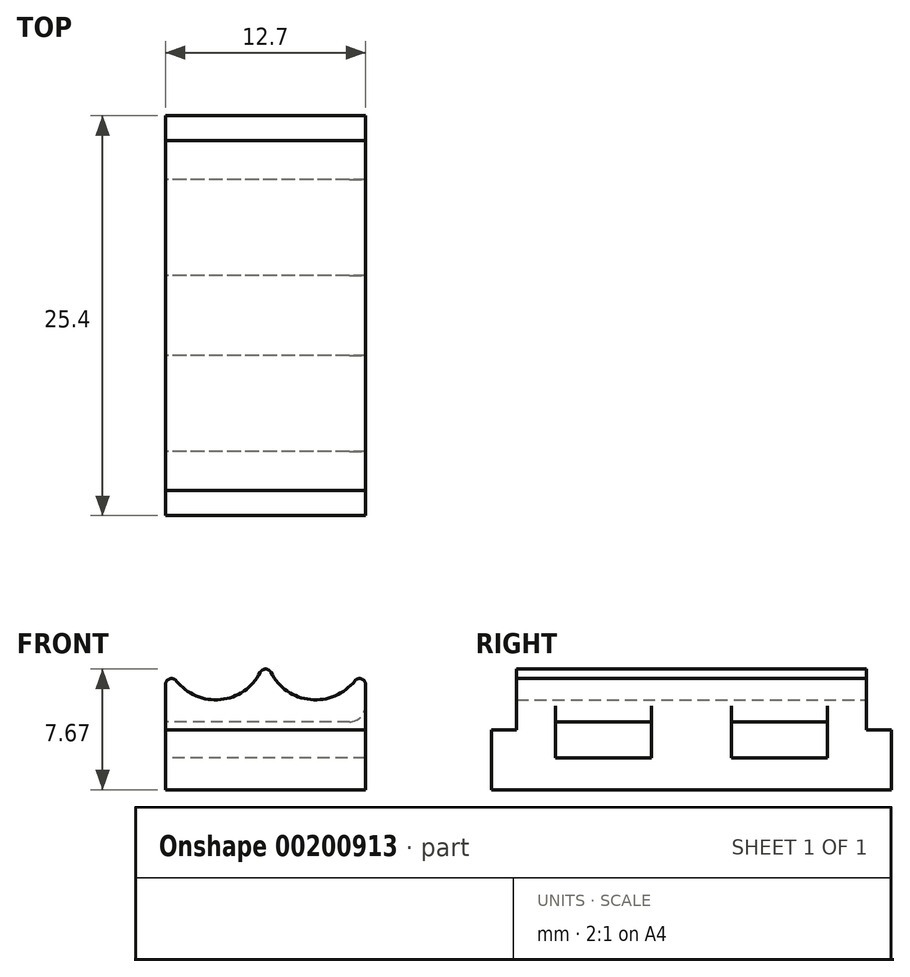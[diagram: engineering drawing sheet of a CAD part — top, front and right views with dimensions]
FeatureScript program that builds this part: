
annotation { "Feature Type Name" : "Feature", "Feature Type Description" : "" }
export const myFeature = defineFeature(function(context is Context, id is Id, definition is map)
    precondition{}
    {
        {
            var Q0;
            Q0=qCreatedBy(makeId("Top.planeOp"),FACE);
            var sketch = newSketch(context, id + "F0", { "sketchPlane" : qUnion([Q0])});
            skLineSegment(sketch, "E0.bottom", {"start": v(6.35, 12.7) * mm, "end": v(-6.35, 12.7) * mm});
            skLineSegment(sketch, "E0.top", {"start": v(6.35, -12.7) * mm, "end": v(-6.35, -12.7) * mm});
            skLineSegment(sketch, "E0.left", {"start": v(6.35, 12.7) * mm, "end": v(6.35, -12.7) * mm});
            skLineSegment(sketch, "E0.right", {"start": v(-6.35, 12.7) * mm, "end": v(-6.35, -12.7) * mm});
            skPoint(sketch, "E0.middle", {"position": v(0, 0) * mm});
            skSolve(sketch);
        }
        {
            var Q0;
            Q0=makeQuery(id+"F0.imprint","IMPRINT",FACE,{"disambiguationData":[TD([[makeQuery(id+"F0.imprint","IMPRINT",EDGE,{"derivedFrom":sQuery(id+"F0.wireOp",EDGE,"E0.bottom")}),1.0]])]});
            extrude(context, id + "F1", {"entities" : qUnion([Q0]), "depth" : 3.8 * mm});
        }
        {
            var Q0;
            Q0=qCreatedBy(makeId("Front.planeOp"),FACE);
            var sketch = newSketch(context, id + "F2", { "sketchPlane" : qUnion([Q0])});
            skArc(sketch, "E1", {"start": v(0, 8.9) * mm, "mid": v(3.18, 5.72) * mm, "end": v(6.35, 8.9) * mm});
            skLineSegment(sketch, "E2", {"start": v(6.35, 8.9) * mm, "end": v(6.35, 3.81) * mm});
            skPoint(sketch, "E3.0", {"position": v(6.35, 3.81) * mm});
            skArc(sketch, "E4.MirrorC", {"start": v(0, 8.9) * mm, "mid": v(-3.18, 5.72) * mm, "end": v(-6.35, 8.9) * mm});
            skLineSegment(sketch, "E5.MirrorCS", {"start": v(-6.35, 8.9) * mm, "end": v(-6.35, 3.81) * mm});
            skLineSegment(sketch, "E6", {"start": v(6.35, 3.81) * mm, "end": v(-6.35, 3.81) * mm});
            skSolve(sketch);
        }
        {
            var Q0;
            Q0=makeQuery(id+"F2.imprint","IMPRINT",FACE,{"disambiguationData":[TD([[makeQuery(id+"F2.imprint","IMPRINT",EDGE,{"derivedFrom":sQuery(id+"F2.wireOp",EDGE,"E1")}),-1.0]])]});
            extrude(context, id + "F3", {"entities" : qUnion([Q0]), "operationType" : NewBodyOperationType.ADD, "endBound" : BoundingType.SYMMETRIC, "depth" : 22.22 * mm});
        }
        {
            var Q0;
            Q0=makeQuery(id+"F3.boolean.opBoolean","MERGE",FACE,{"derivedFrom":[makeQuery(id+"F1.opExtrude","SWEPT_FACE",FACE,{"disambiguationData":[OSD([sQuery(id+"F0.wireOp",EDGE,"E0.right")])]}),makeQuery(id+"F3.opExtrude","SWEPT_FACE",FACE,{"disambiguationData":[OSD([sQuery(id+"F2.wireOp",EDGE,"c90f42b7-518b-497f-ae20-9e41afcd57c50.MirrorCS")])]})]});
            var sketch = newSketch(context, id + "F4", { "sketchPlane" : qUnion([Q0])});
            skLineSegment(sketch, "E7.bottom", {"start": v(-2.54, 2.03) * mm, "end": v(-8.64, 2.03) * mm});
            skLineSegment(sketch, "E7.top", {"start": v(-2.54, 4.32) * mm, "end": v(-8.64, 4.32) * mm});
            skLineSegment(sketch, "E7.left", {"start": v(-2.54, 2.03) * mm, "end": v(-2.54, 4.32) * mm});
            skLineSegment(sketch, "E7.right", {"start": v(-8.64, 2.03) * mm, "end": v(-8.64, 4.32) * mm});
            skPoint(sketch, "E7.middle", {"position": v(-5.59, 3.18) * mm});
            skLineSegment(sketch, "E8.MirrorCS", {"start": v(8.64, 2.03) * mm, "end": v(8.64, 4.32) * mm});
            skLineSegment(sketch, "E9.MirrorCS", {"start": v(2.54, 4.32) * mm, "end": v(8.64, 4.32) * mm});
            skLineSegment(sketch, "E10.MirrorCS", {"start": v(2.54, 2.03) * mm, "end": v(2.54, 4.32) * mm});
            skLineSegment(sketch, "E11.MirrorCS", {"start": v(2.54, 2.03) * mm, "end": v(8.64, 2.03) * mm});
            skSolve(sketch);
        }
        {
            var Q0;
            Q0=makeQuery(id+"F4.imprint","IMPRINT",FACE,{"disambiguationData":[TD([[makeQuery(id+"F4.imprint","IMPRINT",EDGE,{"derivedFrom":sQuery(id+"F4.wireOp",EDGE,"E7.bottom")}),-1.0]])]});
            var Q1;
            Q1=makeQuery(id+"F4.imprint","IMPRINT",FACE,{"disambiguationData":[TD([[makeQuery(id+"F4.imprint","IMPRINT",EDGE,{"derivedFrom":sQuery(id+"F4.wireOp",EDGE,"E8.MirrorCS")}),1.0]])]});
            extrude(context, id + "F5", {"entities" : qUnion([Q0, Q1]), "operationType" : NewBodyOperationType.REMOVE, "oppositeDirection" : true, "depth" : 25.4 * mm});
        }
        {
            var Q0;
            Q0=makeQuery(id+"F3.opExtrude","SWEPT_EDGE",EDGE,{"disambiguationData":[OSD([sQuery(id+"F2.wireOp",EDGE,"E1"),sQuery(id+"F2.wireOp",EDGE,"E2")])]});
            var Q1;
            Q1=makeQuery(id+"F3.opExtrude","SWEPT_EDGE",EDGE,{"disambiguationData":[OSD([sQuery(id+"F2.wireOp",EDGE,"E1"),sQuery(id+"F2.wireOp",EDGE,"E4.MirrorC")])]});
            var Q2;
            Q2=makeQuery(id+"F3.opExtrude","SWEPT_EDGE",EDGE,{"disambiguationData":[OSD([sQuery(id+"F2.wireOp",EDGE,"E4.MirrorC"),sQuery(id+"F2.wireOp",EDGE,"E5.MirrorCS")])]});
            fillet(context, id + "F6", {"entities" : qUnion([Q0, Q1, Q2]), "radius" : 0.38 * mm, "tangentPropagation" : true, "allowEdgeOverflow" : false});
        }
        {
            var Q0;
            Q0=makeQuery(id+"F5.boolean.opBoolean","INTERSECT",EDGE,{"derivedFrom":[makeQuery(id+"F3.boolean.opBoolean","MERGE",FACE,{"derivedFrom":[makeQuery(id+"F1.opExtrude","SWEPT_FACE",FACE,{"disambiguationData":[OSD([sQuery(id+"F0.wireOp",EDGE,"E0.left")])]}),makeQuery(id+"F3.opExtrude","SWEPT_FACE",FACE,{"disambiguationData":[OSD([sQuery(id+"F2.wireOp",EDGE,"E2")])]})]}),makeQuery(id+"F5.opExtrude","SWEPT_FACE",FACE,{"disambiguationData":[OSD([sQuery(id+"F4.wireOp",EDGE,"E7.top")])]})]});
            var Q1;
            Q1=makeQuery(id+"F5.boolean.opBoolean","INTERSECT",EDGE,{"derivedFrom":[makeQuery(id+"F3.boolean.opBoolean","MERGE",FACE,{"derivedFrom":[makeQuery(id+"F1.opExtrude","SWEPT_FACE",FACE,{"disambiguationData":[OSD([sQuery(id+"F0.wireOp",EDGE,"E0.left")])]}),makeQuery(id+"F3.opExtrude","SWEPT_FACE",FACE,{"disambiguationData":[OSD([sQuery(id+"F2.wireOp",EDGE,"E2")])]})]}),makeQuery(id+"F5.opExtrude","SWEPT_FACE",FACE,{"disambiguationData":[OSD([sQuery(id+"F4.wireOp",EDGE,"E9.MirrorCS")])]})]});
            var Q2;
            Q2=makeQuery(id+"F5.boolean.opBoolean","COPY",EDGE,{"derivedFrom":makeQuery(id+"F5.opExtrude","CAP_EDGE",EDGE,{"disambiguationData":[OSD([sQuery(id+"F4.wireOp",EDGE,"E9.MirrorCS")])],"isStart":true})});
            var Q3;
            Q3=makeQuery(id+"F5.boolean.opBoolean","COPY",EDGE,{"derivedFrom":makeQuery(id+"F5.opExtrude","CAP_EDGE",EDGE,{"disambiguationData":[OSD([sQuery(id+"F4.wireOp",EDGE,"E7.top")])],"isStart":true})});
            fillet(context, id + "F7", {"entities" : qUnion([Q0, Q1, Q2, Q3]), "radius" : 1.02 * mm, "tangentPropagation" : true, "allowEdgeOverflow" : false});
        }
    });
